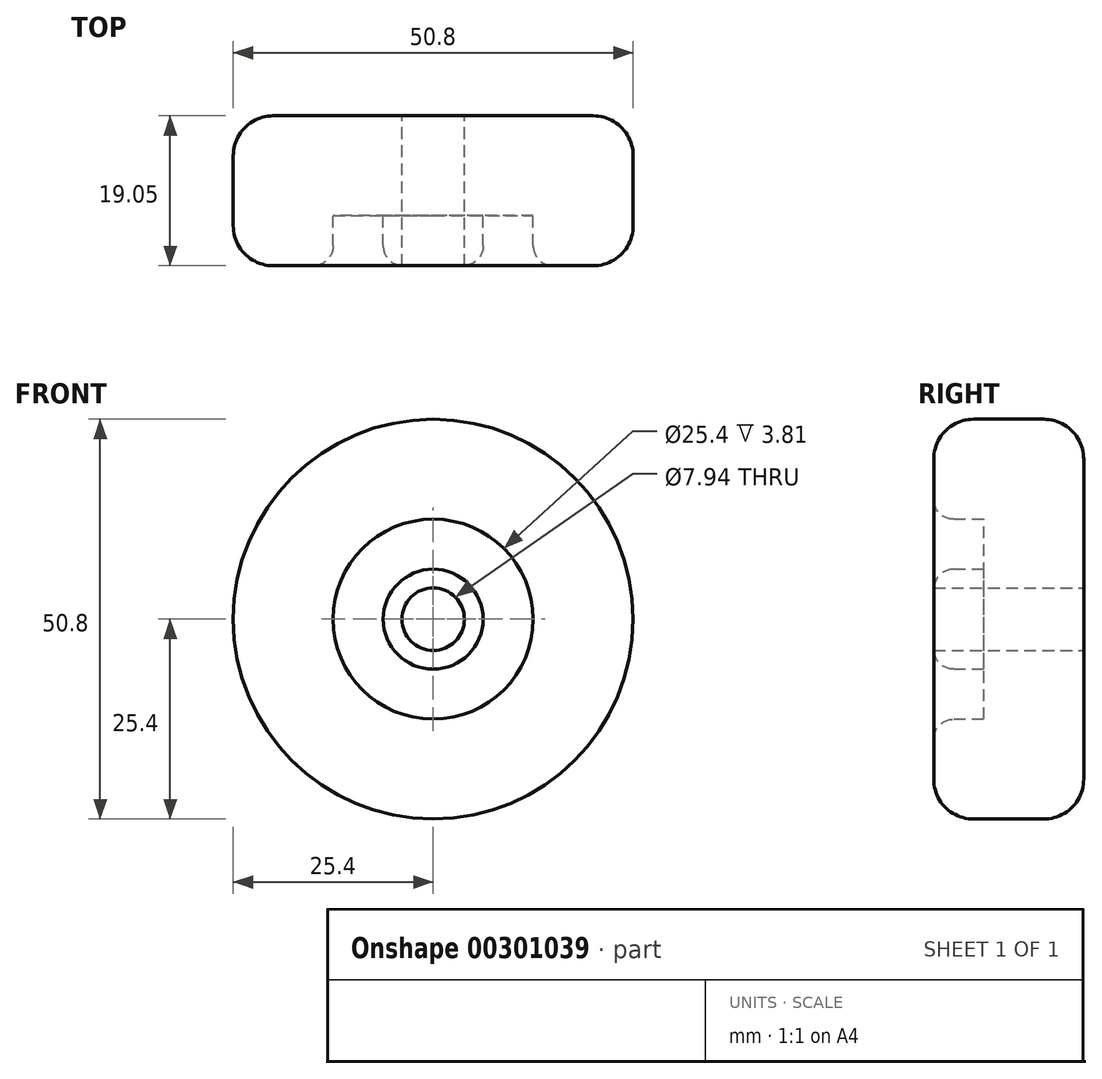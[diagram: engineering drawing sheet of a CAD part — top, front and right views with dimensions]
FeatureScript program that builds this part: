
annotation { "Feature Type Name" : "Feature", "Feature Type Description" : "" }
export const myFeature = defineFeature(function(context is Context, id is Id, definition is map)
    precondition{}
    {
        {
            var Q0;
            Q0=qCreatedBy(makeId("Front.planeOp"),FACE);
            var sketch = newSketch(context, id + "F0", { "sketchPlane" : qUnion([Q0])});
            skCircle(sketch, "E0", {"center": v(0, 0) * mm, "radius": 25.4 * mm});
            skSolve(sketch);
        }
        {
            var Q0;
            Q0=makeQuery(id+"F0.imprint","IMPRINT",FACE,{"disambiguationData":[TD([[makeQuery(id+"F0.imprint","IMPRINT",EDGE,{"derivedFrom":sQuery(id+"F0.wireOp",EDGE,"E0")}),1.0]])]});
            extrude(context, id + "F1", {"entities" : qUnion([Q0]), "depth" : 19.05 * mm});
        }
        {
            var Q0;
            Q0=makeQuery(id+"F1.opExtrude","CAP_EDGE",EDGE,{"disambiguationData":[OSD([sQuery(id+"F0.wireOp",EDGE,"E0")])],"isStart":false});
            var Q1;
            Q1=makeQuery(id+"F1.opExtrude","CAP_EDGE",EDGE,{"disambiguationData":[OSD([sQuery(id+"F0.wireOp",EDGE,"E0")])],"isStart":true});
            fillet(context, id + "F2", {"entities" : qUnion([Q0, Q1]), "radius" : 5.08 * mm, "tangentPropagation" : true, "allowEdgeOverflow" : false});
        }
        {
            var Q0;
            Q0=qCreatedBy(makeId("Front.planeOp"),FACE);
            var sketch = newSketch(context, id + "F3", { "sketchPlane" : qUnion([Q0])});
            skCircle(sketch, "E1", {"center": v(0, 0) * mm, "radius": 12.7 * mm});
            skCircle(sketch, "E2", {"center": v(0, 0) * mm, "radius": 6.35 * mm});
            skSolve(sketch);
        }
        {
            var Q0;
            Q0 = qSketchRegion(id + "F3", true);
            extrude(context, id + "F4", {"entities" : qUnion([Q0]), "operationType" : NewBodyOperationType.REMOVE, "depth" : 25.4 * mm, "hasSecondDirection" : true, "secondDirectionOppositeDirection" : false, "secondDirectionDepth" : 12.7 * mm});
        }
        {
            var Q0;
            Q0=makeQuery(id+"F4.boolean.opBoolean","INTERSECT",EDGE,{"derivedFrom":[makeQuery(id+"F1.opExtrude","CAP_FACE",FACE,{"disambiguationData":[OSD([sQuery(id+"F0.wireOp",EDGE,"E0")])],"isStart":false}),makeQuery(id+"F4.opExtrude","SWEPT_FACE",FACE,{"disambiguationData":[OSD([sQuery(id+"F3.wireOp",EDGE,"E2")])]})]});
            var Q1;
            Q1=makeQuery(id+"F4.boolean.opBoolean","INTERSECT",EDGE,{"derivedFrom":[makeQuery(id+"F1.opExtrude","CAP_FACE",FACE,{"disambiguationData":[OSD([sQuery(id+"F0.wireOp",EDGE,"E0")])],"isStart":false}),makeQuery(id+"F4.opExtrude","SWEPT_FACE",FACE,{"disambiguationData":[OSD([sQuery(id+"F3.wireOp",EDGE,"E1")])]})]});
            fillet(context, id + "F5", {"entities" : qUnion([Q0, Q1]), "radius" : 2.54 * mm, "tangentPropagation" : true, "allowEdgeOverflow" : false});
        }
        {
            var Q0;
            Q0=qCreatedBy(makeId("Front.planeOp"),FACE);
            var sketch = newSketch(context, id + "F6", { "sketchPlane" : qUnion([Q0])});
            skCircle(sketch, "E3", {"center": v(0, 0) * mm, "radius": 3.97 * mm});
            skSolve(sketch);
        }
        {
            var Q0;
            Q0 = qSketchRegion(id + "F6", true);
            extrude(context, id + "F7", {"entities" : qUnion([Q0]), "operationType" : NewBodyOperationType.REMOVE, "endBound" : BoundingType.THROUGH_ALL, "depth" : 25.4 * mm});
        }
    });
